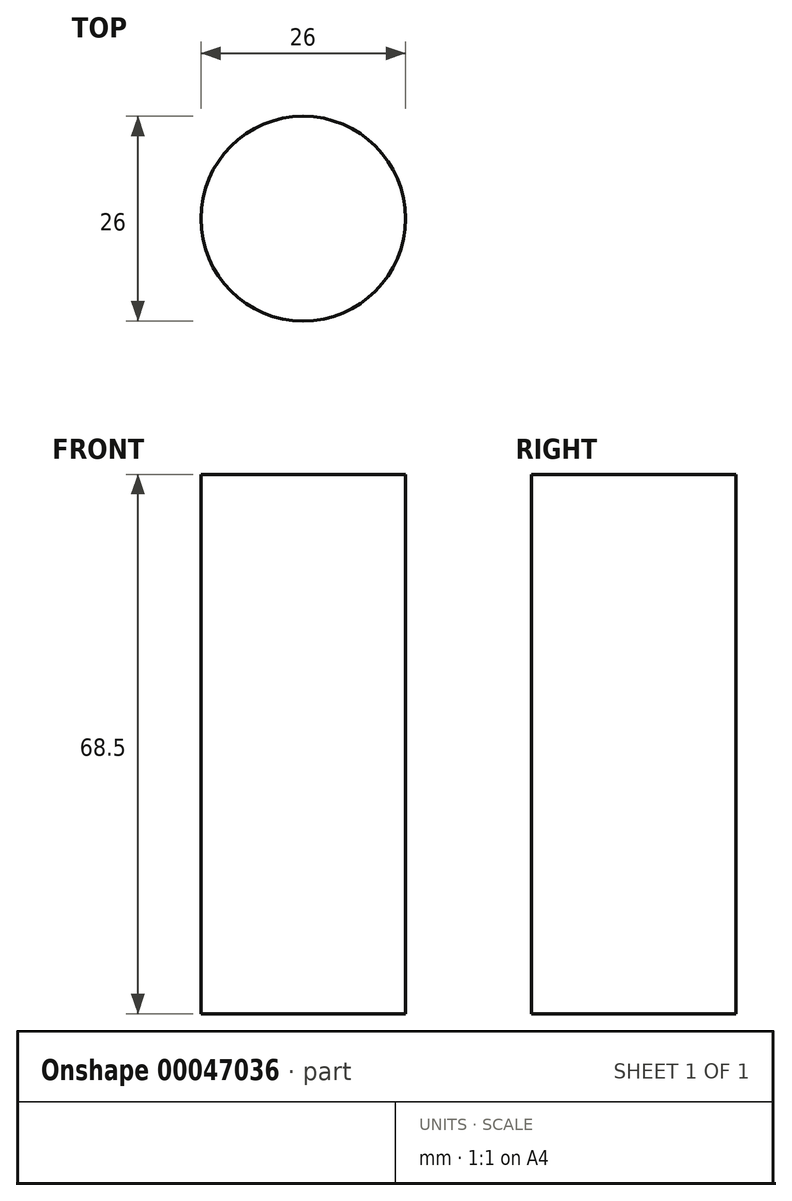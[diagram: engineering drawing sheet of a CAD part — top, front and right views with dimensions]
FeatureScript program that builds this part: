
annotation { "Feature Type Name" : "Feature", "Feature Type Description" : "" }
export const myFeature = defineFeature(function(context is Context, id is Id, definition is map)
    precondition{}
    {
        {
            var Q0;
            Q0=qCreatedBy(makeId("Top.planeOp"),FACE);
            var sketch = newSketch(context, id + "F0", { "sketchPlane" : qUnion([Q0])});
            skCircle(sketch, "E0", {"center": v(0, 0) * mm, "radius": 13 * mm});
            skSolve(sketch);
        }
        {
            var Q0;
            Q0=qSketchRegion(id+"F0",true);
            extrude(context, id + "F1", {"entities" : qUnion([Q0]), "depth" : 68.5 * mm});
        }
    });
